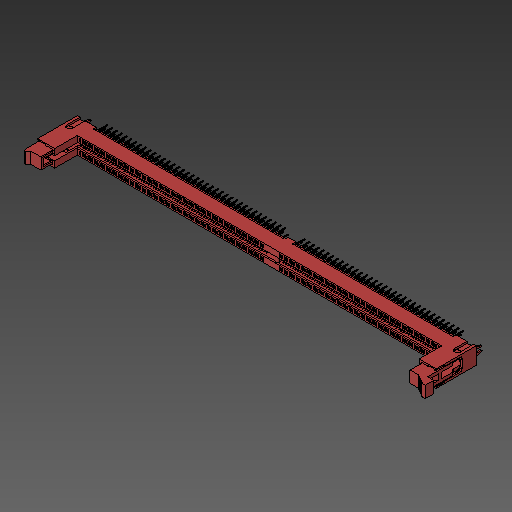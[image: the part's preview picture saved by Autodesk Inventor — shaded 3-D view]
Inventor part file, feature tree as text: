
AUTODESK INVENTOR PART (.ipt)
format: ipt  version: 2018.2 (Build 222227000, 227)  size: 4,003,840 bytes
history: native  units: mm
features: other x1, mirror x1
ambient origin geometry x8: Origin, YZ Plane, XZ Plane, XY Plane, X Axis, Y Axis, Z Axis, Center Point
bodies: Body1 (feature_tree)
feature tree (2):
  other  "ソリッド1"
  mirror  "Mirror2"
